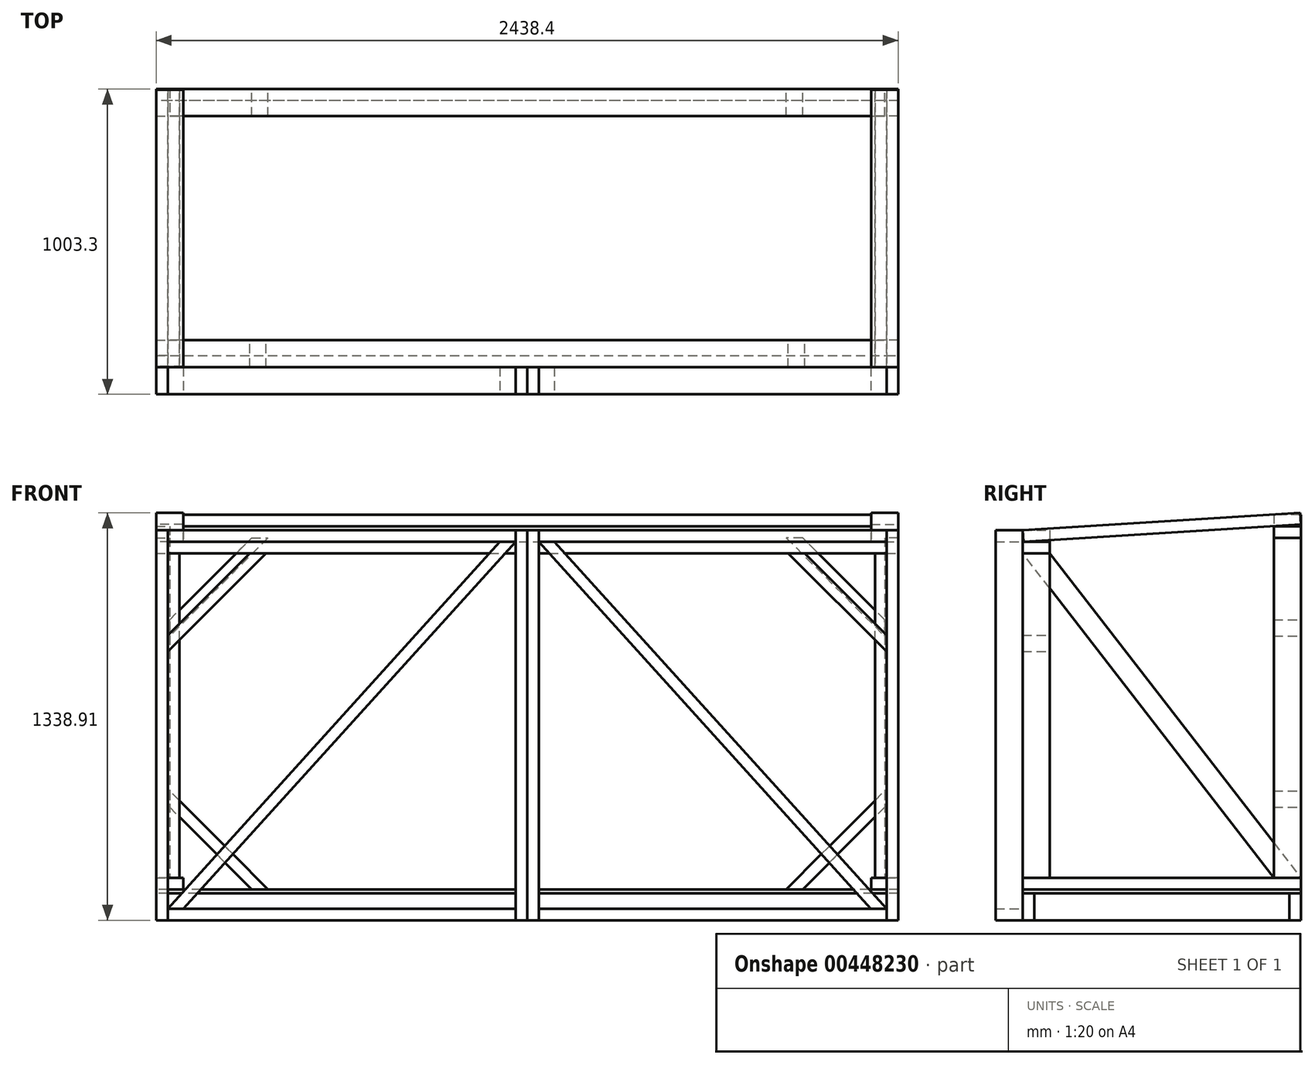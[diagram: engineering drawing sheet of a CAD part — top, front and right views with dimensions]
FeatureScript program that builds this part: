
annotation { "Feature Type Name" : "Feature", "Feature Type Description" : "" }
export const myFeature = defineFeature(function(context is Context, id is Id, definition is map)
    precondition{}
    {
        {
            var Q0;
            Q0=qCreatedBy(makeId("Top.planeOp"),FACE);
            var sketch = newSketch(context, id + "F0", { "sketchPlane" : qUnion([Q0])});
            skLineSegment(sketch, "E0.bottom", {"start": v(1219.2, 457.2) * mm, "end": v(-1219.2, 457.2) * mm});
            skLineSegment(sketch, "E0.top", {"start": v(1219.2, -457.2) * mm, "end": v(-1219.2, -457.2) * mm});
            skLineSegment(sketch, "E0.left", {"start": v(1219.2, 457.2) * mm, "end": v(1219.2, -457.2) * mm});
            skLineSegment(sketch, "E0.right", {"start": v(-1219.2, 457.2) * mm, "end": v(-1219.2, -457.2) * mm});
            skPoint(sketch, "E0.middle", {"position": v(0, 0) * mm});
            skLineSegment(sketch, "E1.bottom", {"start": v(1181.1, 419.1) * mm, "end": v(-1181.1, 419.1) * mm});
            skLineSegment(sketch, "E1.top", {"start": v(1181.1, -419.1) * mm, "end": v(-1181.1, -419.1) * mm});
            skLineSegment(sketch, "E1.left", {"start": v(1181.1, 419.1) * mm, "end": v(1181.1, -419.1) * mm});
            skLineSegment(sketch, "E1.right", {"start": v(-1181.1, 419.1) * mm, "end": v(-1181.1, -419.1) * mm});
            skLineSegment(sketch, "E2", {"start": v(-1181.1, -419.1) * mm, "end": v(-1219.2, -419.1) * mm});
            skLineSegment(sketch, "E3", {"start": v(-1181.1, 419.1) * mm, "end": v(-1219.2, 419.1) * mm});
            skLineSegment(sketch, "E4", {"start": v(1181.1, 419.1) * mm, "end": v(1219.2, 419.1) * mm});
            skLineSegment(sketch, "E5", {"start": v(1181.1, -419.1) * mm, "end": v(1219.2, -419.1) * mm});
            skSolve(sketch);
        }
        {
            var Q0;
            {var subQ1=sQuery(id+"F0.wireOp",EDGE,"E0.bottom");Q0=makeQuery(id+"F0.imprint","IMPRINT",FACE,{"disambiguationData":[TD([[makeQuery(id+"F0.imprint","IMPRINT",EDGE,{"derivedFrom":subQ1}),1.0]])]});}
            var Q1;
            {var subQ1=sQuery(id+"F0.wireOp",EDGE,"E0.top");Q1=makeQuery(id+"F0.imprint","IMPRINT",FACE,{"disambiguationData":[TD([[makeQuery(id+"F0.imprint","IMPRINT",EDGE,{"derivedFrom":subQ1}),-1.0]])]});}
            extrude(context, id + "F1", {"entities" : qUnion([Q0, Q1]), "depth" : 88.9 * mm});
        }
        {
            var Q0;
            Q0=makeQuery(id+"F0.imprint","IMPRINT",FACE,{"disambiguationData":[TD([[makeQuery(id+"F0.imprint","IMPRINT",EDGE,{"derivedFrom":sQuery(id+"F0.wireOp",EDGE,"E1.right")}),-1.0]])]});
            var Q1;
            Q1=makeQuery(id+"F0.imprint","IMPRINT",FACE,{"disambiguationData":[TD([[makeQuery(id+"F0.imprint","IMPRINT",EDGE,{"derivedFrom":sQuery(id+"F0.wireOp",EDGE,"E1.left")}),1.0]])]});
            var Q2;
            {var subQ1=sQuery(id+"F0.wireOp",EDGE,"E0.bottom");Q2=makeQuery(id+"F0.imprint","IMPRINT",FACE,{"disambiguationData":[TD([[makeQuery(id+"F0.imprint","IMPRINT",EDGE,{"derivedFrom":subQ1}),1.0]])]});}
            var Q3;
            Q3=makeQuery(id+"F1.opExtrude","CAP_FACE",FACE,{"disambiguationData":[OSD([sQuery(id+"F0.wireOp",EDGE,"E0.bottom"),sQuery(id+"F0.wireOp",EDGE,"E0.left"),sQuery(id+"F0.wireOp",EDGE,"E0.right"),sQuery(id+"F0.wireOp",EDGE,"E1.bottom"),sQuery(id+"F0.wireOp",EDGE,"E3"),sQuery(id+"F0.wireOp",EDGE,"E4")])],"isStart":false});
            extrude(context, id + "F2", {"entities" : qUnion([Q0, Q1, Q2]), "endBound" : BoundingType.UP_TO_SURFACE, "endBoundEntityFace" : qUnion([Q3]), "depth" : 25.4 * mm});
        }
        {
            var Q0;
            Q0=makeQuery(id+"F1.opExtrude","CAP_FACE",FACE,{"disambiguationData":[OSD([sQuery(id+"F0.wireOp",EDGE,"E0.top"),sQuery(id+"F0.wireOp",EDGE,"E0.left"),sQuery(id+"F0.wireOp",EDGE,"E0.right"),sQuery(id+"F0.wireOp",EDGE,"E1.top"),sQuery(id+"F0.wireOp",EDGE,"E2"),sQuery(id+"F0.wireOp",EDGE,"E5")])],"isStart":false});
            var sketch = newSketch(context, id + "F3", { "sketchPlane" : qUnion([Q0])});
            skLineSegment(sketch, "E6.bottom", {"start": v(-1219.2, -457.2) * mm, "end": v(1219.2, -457.2) * mm});
            skLineSegment(sketch, "E6.top", {"start": v(-1219.2, 457.2) * mm, "end": v(1219.2, 457.2) * mm});
            skLineSegment(sketch, "E6.left", {"start": v(-1219.2, -457.2) * mm, "end": v(-1219.2, 457.2) * mm});
            skLineSegment(sketch, "E6.right", {"start": v(1219.2, -457.2) * mm, "end": v(1219.2, 457.2) * mm});
            skPoint(sketch, "E6.middle", {"position": v(0, 0) * mm});
            skSolve(sketch);
        }
        {
            var Q0;
            Q0 = qSketchRegion(id + "F3", true);
            extrude(context, id + "F4", {"entities" : qUnion([Q0]), "depth" : 12.7 * mm});
        }
        {
            var Q0;
            Q0=makeQuery(id+"F4.opExtrude","CAP_FACE",FACE,{"disambiguationData":[OSD([sQuery(id+"F3.wireOp",EDGE,"E6.bottom"),sQuery(id+"F3.wireOp",EDGE,"E6.top"),sQuery(id+"F3.wireOp",EDGE,"E6.left"),sQuery(id+"F3.wireOp",EDGE,"E6.right")])],"isStart":false});
            var sketch = newSketch(context, id + "F5", { "sketchPlane" : qUnion([Q0])});
            skLineSegment(sketch, "E7.bottom", {"start": v(-1219.2, 457.2) * mm, "end": v(-1130.3, 457.2) * mm});
            skLineSegment(sketch, "E7.top", {"start": v(-1219.2, -457.2) * mm, "end": v(-1130.3, -457.2) * mm});
            skLineSegment(sketch, "E7.left", {"start": v(-1219.2, 457.2) * mm, "end": v(-1219.2, -457.2) * mm});
            skLineSegment(sketch, "E7.right", {"start": v(-1130.3, 457.2) * mm, "end": v(-1130.3, -457.2) * mm});
            skSolve(sketch);
        }
        {
            var Q0;
            Q0 = qSketchRegion(id + "F5", true);
            extrude(context, id + "F6", {"entities" : qUnion([Q0]), "depth" : 38.1 * mm});
        }
        {
            var Q0;
            Q0=makeQuery(id+"F6.opExtrude","CAP_FACE",FACE,{"disambiguationData":[OSD([sQuery(id+"F5.wireOp",EDGE,"E7.bottom"),sQuery(id+"F5.wireOp",EDGE,"E7.top"),sQuery(id+"F5.wireOp",EDGE,"E7.left"),sQuery(id+"F5.wireOp",EDGE,"E7.right")])],"isStart":false});
            var sketch = newSketch(context, id + "F7", { "sketchPlane" : qUnion([Q0])});
            skLineSegment(sketch, "E8.bottom", {"start": v(-1219.2, -457.2) * mm, "end": v(-1181.1, -457.2) * mm});
            skLineSegment(sketch, "E8.top", {"start": v(-1219.2, -368.3) * mm, "end": v(-1181.1, -368.3) * mm});
            skLineSegment(sketch, "E8.left", {"start": v(-1219.2, -457.2) * mm, "end": v(-1219.2, -368.3) * mm});
            skLineSegment(sketch, "E8.right", {"start": v(-1181.1, -457.2) * mm, "end": v(-1181.1, -368.3) * mm});
            skSolve(sketch);
        }
        {
            var Q0;
            Q0 = qSketchRegion(id + "F7", true);
            extrude(context, id + "F8", {"entities" : qUnion([Q0]), "depth" : 1066.8 * mm});
        }
        {
            var Q0;
            Q0=makeQuery(id+"F6.opExtrude","CAP_FACE",FACE,{"disambiguationData":[OSD([sQuery(id+"F5.wireOp",EDGE,"E7.bottom"),sQuery(id+"F5.wireOp",EDGE,"E7.top"),sQuery(id+"F5.wireOp",EDGE,"E7.left"),sQuery(id+"F5.wireOp",EDGE,"E7.right")])],"isStart":false});
            var sketch = newSketch(context, id + "F9", { "sketchPlane" : qUnion([Q0])});
            skPoint(sketch, "E9.oppositeSnap0", {"position": v(-1174.75, 457.2) * mm});
            skLineSegment(sketch, "E9.bottom", {"start": v(-1219.2, 457.2) * mm, "end": v(-1174.75, 457.2) * mm});
            skLineSegment(sketch, "E9.top", {"start": v(-1219.2, 368.3) * mm, "end": v(-1174.75, 368.3) * mm});
            skLineSegment(sketch, "E9.left", {"start": v(-1219.2, 457.2) * mm, "end": v(-1219.2, 368.3) * mm});
            skLineSegment(sketch, "E9.right", {"start": v(-1174.75, 457.2) * mm, "end": v(-1174.75, 368.3) * mm});
            skSolve(sketch);
        }
        {
            var Q0;
            Q0=makeQuery(id+"F9.imprint","IMPRINT",FACE,{"disambiguationData":[TD([[makeQuery(id+"F9.imprint","IMPRINT",EDGE,{"derivedFrom":sQuery(id+"F9.wireOp",EDGE,"E9.bottom")}),-1.0]])]});
            extrude(context, id + "F10", {"entities" : qUnion([Q0]), "depth" : 1117.6 * mm});
        }
        {
            var Q0;
            Q0=makeQuery(id+"F10.opExtrude","SWEPT_BODY",BODY,{"disambiguationData":[OSD([sQuery(id+"F9.wireOp",EDGE,"E9.bottom"),sQuery(id+"F9.wireOp",EDGE,"E9.top"),sQuery(id+"F9.wireOp",EDGE,"E9.left"),sQuery(id+"F9.wireOp",EDGE,"E9.right")])]});
            var Q1;
            Q1=makeQuery(id+"F8.opExtrude","SWEPT_BODY",BODY,{"disambiguationData":[OSD([sQuery(id+"F7.wireOp",EDGE,"E8.bottom"),sQuery(id+"F7.wireOp",EDGE,"E8.top"),sQuery(id+"F7.wireOp",EDGE,"E8.left"),sQuery(id+"F7.wireOp",EDGE,"E8.right")])]});
            var Q2;
            Q2=qCreatedBy(makeId("Right.planeOp"),FACE);
            mirror(context, id + "F11", {"entities" : qUnion([Q0, Q1]), "mirrorPlane" : qUnion([Q2])});
        }
        {
            var Q0;
            Q0=makeQuery(id+"F8.opExtrude","CAP_FACE",FACE,{"disambiguationData":[OSD([sQuery(id+"F7.wireOp",EDGE,"E8.bottom"),sQuery(id+"F7.wireOp",EDGE,"E8.top"),sQuery(id+"F7.wireOp",EDGE,"E8.left"),sQuery(id+"F7.wireOp",EDGE,"E8.right")])],"isStart":false});
            var sketch = newSketch(context, id + "F12", { "sketchPlane" : qUnion([Q0])});
            skLineSegment(sketch, "E10.bottom", {"start": v(-1219.2, -457.2) * mm, "end": v(1219.2, -457.2) * mm});
            skLineSegment(sketch, "E10.top", {"start": v(-1219.2, -368.3) * mm, "end": v(1219.2, -368.3) * mm});
            skLineSegment(sketch, "E10.left", {"start": v(-1219.2, -457.2) * mm, "end": v(-1219.2, -368.3) * mm});
            skLineSegment(sketch, "E10.right", {"start": v(1219.2, -457.2) * mm, "end": v(1219.2, -368.3) * mm});
            skSolve(sketch);
        }
        {
            var Q0;
            {var subQ2=sQuery(id+"F12.wireOp",EDGE,"E10.right");Q0=makeQuery(id+"F12.imprint","IMPRINT",FACE,{"disambiguationData":[TD([[makeQuery(id+"F12.imprint","IMPRINT",EDGE,{"derivedFrom":subQ2}),1.0]])]});}
            var Q1;
            {var subQ0=sQuery(id+"F12.wireOp",EDGE,"E10.left");Q1=makeQuery(id+"F12.imprint","IMPRINT",FACE,{"disambiguationData":[TD([[makeQuery(id+"F12.imprint","IMPRINT",EDGE,{"derivedFrom":subQ0}),1.0]])]});}
            extrude(context, id + "F13", {"entities" : qUnion([Q0, Q1]), "depth" : 38.1 * mm});
        }
        {
            var Q0;
            Q0=makeQuery(id+"F10.opExtrude","CAP_FACE",FACE,{"disambiguationData":[OSD([sQuery(id+"F9.wireOp",EDGE,"E9.bottom"),sQuery(id+"F9.wireOp",EDGE,"E9.top"),sQuery(id+"F9.wireOp",EDGE,"E9.left"),sQuery(id+"F9.wireOp",EDGE,"E9.right")])],"isStart":false});
            var sketch = newSketch(context, id + "F14", { "sketchPlane" : qUnion([Q0])});
            skLineSegment(sketch, "E11.bottom", {"start": v(-1219.2, 457.2) * mm, "end": v(1219.2, 457.2) * mm});
            skLineSegment(sketch, "E11.top", {"start": v(-1219.2, 368.3) * mm, "end": v(1219.2, 368.3) * mm});
            skLineSegment(sketch, "E11.left", {"start": v(-1219.2, 457.2) * mm, "end": v(-1219.2, 368.3) * mm});
            skLineSegment(sketch, "E11.right", {"start": v(1219.2, 457.2) * mm, "end": v(1219.2, 368.3) * mm});
            skSolve(sketch);
        }
        {
            var Q0;
            Q0 = qSketchRegion(id + "F14", true);
            var sketch = newSketch(context, id + "F15", { "sketchPlane" : qUnion([Q0])});
            skSolve(sketch);
        }
        {
            var Q0;
            {var subQ2=sQuery(id+"F14.wireOp",EDGE,"E11.right");Q0=makeQuery(id+"F15.imprint","IMPRINT",FACE,{"disambiguationData":[TD([[makeQuery(id+"F15.imprint","IMPRINT",EDGE,{"derivedFrom":makeQuery(id+"F14.imprint","IMPRINT",EDGE,{"derivedFrom":subQ2})}),-1.0]])]});}
            var Q1;
            {var subQ0=sQuery(id+"F14.wireOp",EDGE,"E11.left");Q1=makeQuery(id+"F15.imprint","IMPRINT",FACE,{"disambiguationData":[TD([[makeQuery(id+"F15.imprint","IMPRINT",EDGE,{"derivedFrom":makeQuery(id+"F14.imprint","IMPRINT",EDGE,{"derivedFrom":subQ0})}),1.0]])]});}
            extrude(context, id + "F16", {"entities" : qUnion([Q0, Q1]), "depth" : 38.1 * mm});
        }
        {
            var Q0;
            Q0=makeQuery(id+"F8.opExtrude","SWEPT_FACE",FACE,{"disambiguationData":[OSD([sQuery(id+"F7.wireOp",EDGE,"E8.left")])]});
            var sketch = newSketch(context, id + "F17", { "sketchPlane" : qUnion([Q0])});
            skLineSegment(sketch, "E12", {"start": v(454.85, 1244.6) * mm, "end": v(-457.2, 1300.89) * mm});
            skLineSegment(sketch, "E13", {"start": v(-457.2, 1300.89) * mm, "end": v(-454.85, 1338.91) * mm});
            skLineSegment(sketch, "E14", {"start": v(-454.85, 1338.91) * mm, "end": v(457.2, 1282.63) * mm});
            skLineSegment(sketch, "E15", {"start": v(457.2, 1282.63) * mm, "end": v(454.85, 1244.6) * mm});
            skSolve(sketch);
        }
        {
            var Q0;
            Q0 = qSketchRegion(id + "F17", true);
            extrude(context, id + "F18", {"entities" : qUnion([Q0]), "oppositeDirection" : true, "depth" : 88.9 * mm});
        }
        {
            var Q0;
            Q0=makeQuery(id+"F18.opExtrude","SWEPT_BODY",BODY,{"disambiguationData":[OSD([sQuery(id+"F17.wireOp",EDGE,"E12"),sQuery(id+"F17.wireOp",EDGE,"E13"),sQuery(id+"F17.wireOp",EDGE,"E14"),sQuery(id+"F17.wireOp",EDGE,"E15")])]});
            var Q1;
            Q1=makeQuery(id+"F6.opExtrude","SWEPT_BODY",BODY,{"disambiguationData":[OSD([sQuery(id+"F5.wireOp",EDGE,"E7.bottom"),sQuery(id+"F5.wireOp",EDGE,"E7.top"),sQuery(id+"F5.wireOp",EDGE,"E7.left"),sQuery(id+"F5.wireOp",EDGE,"E7.right")])]});
            var Q2;
            Q2=qCreatedBy(makeId("Right.planeOp"),FACE);
            mirror(context, id + "F19", {"entities" : qUnion([Q0, Q1]), "mirrorPlane" : qUnion([Q2])});
        }
        {
            var Q0;
            Q0=makeQuery(id+"F1.opExtrude","SWEPT_FACE",FACE,{"disambiguationData":[OSD([sQuery(id+"F0.wireOp",EDGE,"E0.top")])]});
            var sketch = newSketch(context, id + "F20", { "sketchPlane" : qUnion([Q0])});
            skLineSegment(sketch, "E16.bottom", {"start": v(-1219.2, 0) * mm, "end": v(0, 0) * mm});
            skLineSegment(sketch, "E16.top", {"start": v(-1219.2, 1282.63) * mm, "end": v(0, 1282.63) * mm});
            skLineSegment(sketch, "E16.left", {"start": v(-1219.2, 0) * mm, "end": v(-1219.2, 1282.63) * mm});
            skLineSegment(sketch, "E16.right", {"start": v(0, 0) * mm, "end": v(0, 1282.63) * mm});
            skLineSegment(sketch, "E17", {"start": v(-38.1, 1282.63) * mm, "end": v(-38.1, 0) * mm});
            skLineSegment(sketch, "E18", {"start": v(-1181.1, 0) * mm, "end": v(-1181.1, 1282.63) * mm});
            skLineSegment(sketch, "E19", {"start": v(-38.1, 1244.53) * mm, "end": v(-1181.1, 1244.53) * mm});
            skLineSegment(sketch, "E20", {"start": v(-38.1, 38.1) * mm, "end": v(-1181.1, 38.1) * mm});
            skSolve(sketch);
        }
        {
            var Q0;
            {var subQ1=sQuery(id+"F20.wireOp",EDGE,"E16.top");var subQ4=sQuery(id+"F20.wireOp",EDGE,"E16.left");var subQ7=makeQuery(id+"F20.imprint","INTERSECT",VERTEX,{"derivedFrom":[subQ1,subQ4]});Q0=makeQuery(id+"F20.imprint","IMPRINT",FACE,{"disambiguationData":[TD([[makeQuery(id+"F20.imprint","IMPRINT",EDGE,{"disambiguationData":[TD([[subQ7,-1.0]])],"derivedFrom":subQ1}),-1.0]])]});}
            var Q1;
            {var subQ4=sQuery(id+"F20.wireOp",EDGE,"E16.bottom");var subQ6=sQuery(id+"F20.wireOp",EDGE,"E16.left");var subQ7=makeQuery(id+"F20.imprint","INTERSECT",VERTEX,{"derivedFrom":[subQ4,subQ6]});Q1=makeQuery(id+"F20.imprint","IMPRINT",FACE,{"disambiguationData":[TD([[makeQuery(id+"F20.imprint","IMPRINT",EDGE,{"disambiguationData":[TD([[subQ7,1.0]])],"derivedFrom":subQ4}),-1.0]])]});}
            var Q2;
            {var subQ4=sQuery(id+"F20.wireOp",EDGE,"E16.right");var subQ5=sQuery(id+"F20.wireOp",EDGE,"E16.top");var subQ6=makeQuery(id+"F20.imprint","INTERSECT",VERTEX,{"derivedFrom":[subQ5,subQ4]});Q2=makeQuery(id+"F20.imprint","IMPRINT",FACE,{"disambiguationData":[TD([[makeQuery(id+"F20.imprint","IMPRINT",EDGE,{"disambiguationData":[TD([[subQ6,1.0]])],"derivedFrom":subQ5}),-1.0]])]});}
            var Q3;
            {var subQ0=sQuery(id+"F20.wireOp",EDGE,"E17");var subQ1=makeQuery(id+"F20.imprint","INTERSECT",VERTEX,{"derivedFrom":[subQ0,sQuery(id+"F20.wireOp",EDGE,"E20")]});Q3=makeQuery(id+"F20.imprint","IMPRINT",FACE,{"disambiguationData":[TD([[makeQuery(id+"F20.imprint","IMPRINT",EDGE,{"disambiguationData":[TD([[subQ1,1.0]])],"derivedFrom":subQ0}),1.0]])]});}
            extrude(context, id + "F21", {"entities" : qUnion([Q0, Q1, Q2, Q3]), "depth" : 88.9 * mm});
        }
        {
            var Q0;
            {var subQ5=sQuery(id+"F20.wireOp",EDGE,"E19");Q0=makeQuery(id+"F20.imprint","IMPRINT",FACE,{"disambiguationData":[TD([[makeQuery(id+"F20.imprint","IMPRINT",EDGE,{"derivedFrom":subQ5}),-1.0]])]});}
            var Q1;
            {var subQ5=sQuery(id+"F20.wireOp",EDGE,"E20");Q1=makeQuery(id+"F20.imprint","IMPRINT",FACE,{"disambiguationData":[TD([[makeQuery(id+"F20.imprint","IMPRINT",EDGE,{"derivedFrom":subQ5}),1.0]])]});}
            var Q2;
            Q2=makeQuery(id+"F21.opExtrude","CAP_FACE",FACE,{"disambiguationData":[OSD([sQuery(id+"F20.wireOp",EDGE,"E16.bottom"),sQuery(id+"F20.wireOp",EDGE,"E16.top"),sQuery(id+"F20.wireOp",EDGE,"E16.left"),sQuery(id+"F20.wireOp",EDGE,"E18")])],"isStart":false});
            extrude(context, id + "F22", {"entities" : qUnion([Q0, Q1]), "endBound" : BoundingType.UP_TO_SURFACE, "endBoundEntityFace" : qUnion([Q2]), "depth" : 25.4 * mm});
        }
        {
            var Q0;
            Q0=makeQuery(id+"F22.opExtrude","CAP_FACE",FACE,{"disambiguationData":[OSD([sQuery(id+"F20.wireOp",EDGE,"E16.top"),sQuery(id+"F20.wireOp",EDGE,"E17"),sQuery(id+"F20.wireOp",EDGE,"E18"),sQuery(id+"F20.wireOp",EDGE,"E19")])],"isStart":false});
            var sketch = newSketch(context, id + "F23", { "sketchPlane" : qUnion([Q0])});
            skLineSegment(sketch, "E21", {"start": v(-89.48, 1244.53) * mm, "end": v(-1181.1, 38.1) * mm});
            skLineSegment(sketch, "E22", {"start": v(-1181.1, 38.1) * mm, "end": v(-1129.72, 38.1) * mm});
            skLineSegment(sketch, "E23", {"start": v(-1129.72, 38.1) * mm, "end": v(-38.1, 1244.53) * mm});
            skLineSegment(sketch, "E24", {"start": v(-38.1, 1244.53) * mm, "end": v(-89.48, 1244.53) * mm});
            skSolve(sketch);
        }
        {
            var Q0;
            Q0 = qSketchRegion(id + "F23", true);
            var Q1;
            Q1=makeQuery(id+"F21.opExtrude","CAP_FACE",FACE,{"disambiguationData":[OSD([sQuery(id+"F20.wireOp",EDGE,"E16.bottom"),sQuery(id+"F20.wireOp",EDGE,"E16.top"),sQuery(id+"F20.wireOp",EDGE,"E16.right"),sQuery(id+"F20.wireOp",EDGE,"E17")])],"isStart":true});
            extrude(context, id + "F24", {"entities" : qUnion([Q0]), "endBound" : BoundingType.UP_TO_SURFACE, "oppositeDirection" : true, "endBoundEntityFace" : qUnion([Q1]), "depth" : 25.4 * mm});
        }
        {
            var Q0;
            Q0=makeQuery(id+"F21.opExtrude","SWEPT_BODY",BODY,{"disambiguationData":[OSD([sQuery(id+"F20.wireOp",EDGE,"E16.bottom"),sQuery(id+"F20.wireOp",EDGE,"E16.top"),sQuery(id+"F20.wireOp",EDGE,"E16.left"),sQuery(id+"F20.wireOp",EDGE,"E18")])]});
            var Q1;
            Q1=makeQuery(id+"F22.opExtrude","SWEPT_BODY",BODY,{"disambiguationData":[OSD([sQuery(id+"F20.wireOp",EDGE,"E16.top"),sQuery(id+"F20.wireOp",EDGE,"E17"),sQuery(id+"F20.wireOp",EDGE,"E18"),sQuery(id+"F20.wireOp",EDGE,"E19")])]});
            var Q2;
            Q2=makeQuery(id+"F24.opExtrude","SWEPT_BODY",BODY,{"disambiguationData":[OSD([sQuery(id+"F23.wireOp",EDGE,"E21"),sQuery(id+"F23.wireOp",EDGE,"E22"),sQuery(id+"F23.wireOp",EDGE,"E23"),sQuery(id+"F23.wireOp",EDGE,"E24")])]});
            var Q3;
            Q3=makeQuery(id+"F21.opExtrude","SWEPT_BODY",BODY,{"disambiguationData":[OSD([sQuery(id+"F20.wireOp",EDGE,"E16.bottom"),sQuery(id+"F20.wireOp",EDGE,"E16.top"),sQuery(id+"F20.wireOp",EDGE,"E16.right"),sQuery(id+"F20.wireOp",EDGE,"E17")])]});
            var Q4;
            Q4=makeQuery(id+"F22.opExtrude","SWEPT_BODY",BODY,{"disambiguationData":[OSD([sQuery(id+"F20.wireOp",EDGE,"E16.bottom"),sQuery(id+"F20.wireOp",EDGE,"E17"),sQuery(id+"F20.wireOp",EDGE,"E18"),sQuery(id+"F20.wireOp",EDGE,"E20")])]});
            var Q5;
            Q5=qCreatedBy(makeId("Right.planeOp"),FACE);
            mirror(context, id + "F25", {"entities" : qUnion([Q0, Q1, Q2, Q3, Q4]), "mirrorPlane" : qUnion([Q5])});
        }
        {
            var Q0;
            Q0=makeQuery(id+"F8.opExtrude","SWEPT_FACE",FACE,{"disambiguationData":[OSD([sQuery(id+"F7.wireOp",EDGE,"E8.right")])]});
            var sketch = newSketch(context, id + "F26", { "sketchPlane" : qUnion([Q0])});
            skLineSegment(sketch, "E25", {"start": v(-368.3, 1206.5) * mm, "end": v(457.2, 139.7) * mm});
            skLineSegment(sketch, "E26", {"start": v(457.2, 139.7) * mm, "end": v(368.3, 139.7) * mm});
            skLineSegment(sketch, "E27", {"start": v(368.3, 139.7) * mm, "end": v(-457.2, 1206.5) * mm});
            skLineSegment(sketch, "E28", {"start": v(-457.2, 1206.5) * mm, "end": v(-368.3, 1206.5) * mm});
            skSolve(sketch);
        }
        {
            var Q0;
            {var subQ0=sQuery(id+"F26.wireOp",EDGE,"E25");Q0=makeQuery(id+"F26.imprint","IMPRINT",FACE,{"disambiguationData":[TD([[makeQuery(id+"F26.imprint","IMPRINT",EDGE,{"derivedFrom":subQ0}),-1.0]])]});}
            var Q1;
            {var subQ0=sQuery(id+"F26.wireOp",EDGE,"E28");Q1=makeQuery(id+"F26.imprint","IMPRINT",FACE,{"disambiguationData":[TD([[makeQuery(id+"F26.imprint","IMPRINT",EDGE,{"derivedFrom":subQ0}),-1.0]])]});}
            extrude(context, id + "F27", {"entities" : qUnion([Q0, Q1]), "depth" : 38.1 * mm});
        }
        {
            var Q0;
            Q0=makeQuery(id+"F10.opExtrude","SWEPT_FACE",FACE,{"disambiguationData":[OSD([sQuery(id+"F9.wireOp",EDGE,"E9.bottom")])]});
            var sketch = newSketch(context, id + "F28", { "sketchPlane" : qUnion([Q0])});
            skLineSegment(sketch, "E29", {"start": v(1174.75, 371) * mm, "end": v(905.34, 101.6) * mm});
            skLineSegment(sketch, "E30", {"start": v(905.34, 101.6) * mm, "end": v(851.46, 101.6) * mm});
            skLineSegment(sketch, "E31", {"start": v(851.46, 101.6) * mm, "end": v(1174.75, 424.89) * mm});
            skLineSegment(sketch, "E32", {"start": v(1174.75, 424.89) * mm, "end": v(1174.75, 371) * mm});
            skSolve(sketch);
        }
        {
            var Q0;
            Q0=makeQuery(id+"F28.imprint","IMPRINT",FACE,{"disambiguationData":[TD([[makeQuery(id+"F28.imprint","IMPRINT",EDGE,{"derivedFrom":sQuery(id+"F28.wireOp",EDGE,"E29")}),-1.0]])]});
            extrude(context, id + "F29", {"entities" : qUnion([Q0]), "oppositeDirection" : true, "depth" : 88.9 * mm});
        }
        {
            var Q0;
            Q0=makeQuery(id+"F27.opExtrude","SWEPT_BODY",BODY,{"disambiguationData":[OSD([sQuery(id+"F7.wireOp",EDGE,"E8.top"),sQuery(id+"F7.wireOp",EDGE,"E8.right"),sQuery(id+"F26.wireOp",EDGE,"E25"),sQuery(id+"F26.wireOp",EDGE,"E26"),sQuery(id+"F26.wireOp",EDGE,"E27")])]});
            var Q1;
            Q1=makeQuery(id+"F29.opExtrude","SWEPT_BODY",BODY,{"disambiguationData":[OSD([sQuery(id+"F28.wireOp",EDGE,"E29"),sQuery(id+"F28.wireOp",EDGE,"E30"),sQuery(id+"F28.wireOp",EDGE,"E31"),sQuery(id+"F28.wireOp",EDGE,"E32")])]});
            var Q2;
            Q2=qCreatedBy(makeId("Right.planeOp"),FACE);
            mirror(context, id + "F30", {"entities" : qUnion([Q0, Q1]), "mirrorPlane" : qUnion([Q2])});
        }
        {
            var Q0;
            {var subQ2=sQuery(id+"F14.wireOp",EDGE,"E11.right");Q0=makeQuery(id+"F14.imprint","IMPRINT",FACE,{"disambiguationData":[TD([[makeQuery(id+"F14.imprint","IMPRINT",EDGE,{"derivedFrom":subQ2}),-1.0]])]});}
            var Q1;
            Q1=makeQuery(id+"F4.opExtrude","CAP_FACE",FACE,{"disambiguationData":[OSD([sQuery(id+"F3.wireOp",EDGE,"E6.bottom"),sQuery(id+"F3.wireOp",EDGE,"E6.top"),sQuery(id+"F3.wireOp",EDGE,"E6.left"),sQuery(id+"F3.wireOp",EDGE,"E6.right")])],"isStart":false});
            cPlane(context, id + "F31", {"entities" : qUnion([Q0, Q1]), "cplaneType" : CPlaneType.MID_PLANE, "offset" : 25.4 * mm, "width" : 152.4 * mm, "height" : 152.4 * mm});
        }
        {
            var Q0;
            Q0=makeQuery(id+"F30.opPattern","COPY",BODY,{"derivedFrom":makeQuery(id+"F29.opExtrude","SWEPT_BODY",BODY,{"disambiguationData":[OSD([sQuery(id+"F28.wireOp",EDGE,"E29"),sQuery(id+"F28.wireOp",EDGE,"E30"),sQuery(id+"F28.wireOp",EDGE,"E31"),sQuery(id+"F28.wireOp",EDGE,"E32")])]}),"instanceName":"1"});
            var Q1;
            Q1=makeQuery(id+"F29.opExtrude","SWEPT_BODY",BODY,{"disambiguationData":[OSD([sQuery(id+"F28.wireOp",EDGE,"E29"),sQuery(id+"F28.wireOp",EDGE,"E30"),sQuery(id+"F28.wireOp",EDGE,"E31"),sQuery(id+"F28.wireOp",EDGE,"E32")])]});
            var Q2;
            Q2=qCreatedBy(id+"F31.planeOp",FACE);
            mirror(context, id + "F32", {"entities" : qUnion([Q0, Q1]), "mirrorPlane" : qUnion([Q2])});
        }
        {
            var Q0;
            Q0=makeQuery(id+"F16.opExtrude","CAP_FACE",FACE,{"disambiguationData":[OSD([sQuery(id+"F14.wireOp",EDGE,"E11.bottom"),sQuery(id+"F14.wireOp",EDGE,"E11.top"),sQuery(id+"F14.wireOp",EDGE,"E11.left"),sQuery(id+"F14.wireOp",EDGE,"E11.right")])],"isStart":false});
            var sketch = newSketch(context, id + "F33", { "sketchPlane" : qUnion([Q0])});
            skLineSegment(sketch, "E33.bottom", {"start": v(-1130.3, 457.2) * mm, "end": v(1130.3, 457.2) * mm});
            skLineSegment(sketch, "E33.top", {"start": v(-1130.3, 368.3) * mm, "end": v(1130.3, 368.3) * mm});
            skLineSegment(sketch, "E33.left", {"start": v(-1130.3, 457.2) * mm, "end": v(-1130.3, 368.3) * mm});
            skLineSegment(sketch, "E33.right", {"start": v(1130.3, 457.2) * mm, "end": v(1130.3, 368.3) * mm});
            skSolve(sketch);
        }
        {
            var Q0;
            Q0 = qSketchRegion(id + "F33", true);
            extrude(context, id + "F34", {"entities" : qUnion([Q0]), "depth" : 38.1 * mm});
        }
        {
            var Q0;
            Q0=makeQuery(id+"F13.opExtrude","CAP_FACE",FACE,{"disambiguationData":[OSD([sQuery(id+"F12.wireOp",EDGE,"E10.bottom"),sQuery(id+"F12.wireOp",EDGE,"E10.top"),sQuery(id+"F12.wireOp",EDGE,"E10.left"),sQuery(id+"F12.wireOp",EDGE,"E10.right")])],"isStart":false});
            var sketch = newSketch(context, id + "F35", { "sketchPlane" : qUnion([Q0])});
            skLineSegment(sketch, "E34.bottom", {"start": v(-1130.3, -457.2) * mm, "end": v(1130.3, -457.2) * mm});
            skLineSegment(sketch, "E34.top", {"start": v(-1130.3, -368.3) * mm, "end": v(1130.3, -368.3) * mm});
            skLineSegment(sketch, "E34.left", {"start": v(-1130.3, -457.2) * mm, "end": v(-1130.3, -368.3) * mm});
            skLineSegment(sketch, "E34.right", {"start": v(1130.3, -457.2) * mm, "end": v(1130.3, -368.3) * mm});
            skSolve(sketch);
        }
        {
            var Q0;
            Q0 = qSketchRegion(id + "F35", true);
            extrude(context, id + "F36", {"entities" : qUnion([Q0]), "depth" : 38.1 * mm});
        }
        {
            var Q0;
            Q0=makeQuery(id+"F13.opExtrude","SWEPT_FACE",FACE,{"disambiguationData":[OSD([sQuery(id+"F12.wireOp",EDGE,"E10.top")])]});
            var sketch = newSketch(context, id + "F37", { "sketchPlane" : qUnion([Q0])});
            skLineSegment(sketch, "E35", {"start": v(-857.81, 1206.5) * mm, "end": v(-1181.1, 883.21) * mm});
            skLineSegment(sketch, "E36", {"start": v(-1181.1, 883.21) * mm, "end": v(-1181.1, 937.1) * mm});
            skLineSegment(sketch, "E37", {"start": v(-1181.1, 937.1) * mm, "end": v(-911.7, 1206.5) * mm});
            skLineSegment(sketch, "E38", {"start": v(-911.7, 1206.5) * mm, "end": v(-857.81, 1206.5) * mm});
            skSolve(sketch);
        }
        {
            var Q0;
            Q0 = qSketchRegion(id + "F37", true);
            extrude(context, id + "F38", {"entities" : qUnion([Q0]), "oppositeDirection" : true, "depth" : 88.9 * mm});
        }
        {
            var Q0;
            Q0=makeQuery(id+"F38.opExtrude","SWEPT_BODY",BODY,{"disambiguationData":[OSD([sQuery(id+"F37.wireOp",EDGE,"E35"),sQuery(id+"F37.wireOp",EDGE,"E36"),sQuery(id+"F37.wireOp",EDGE,"E37"),sQuery(id+"F37.wireOp",EDGE,"E38")])]});
            var Q1;
            Q1=qCreatedBy(makeId("Right.planeOp"),FACE);
            mirror(context, id + "F39", {"entities" : qUnion([Q0]), "mirrorPlane" : qUnion([Q1])});
        }
    });
